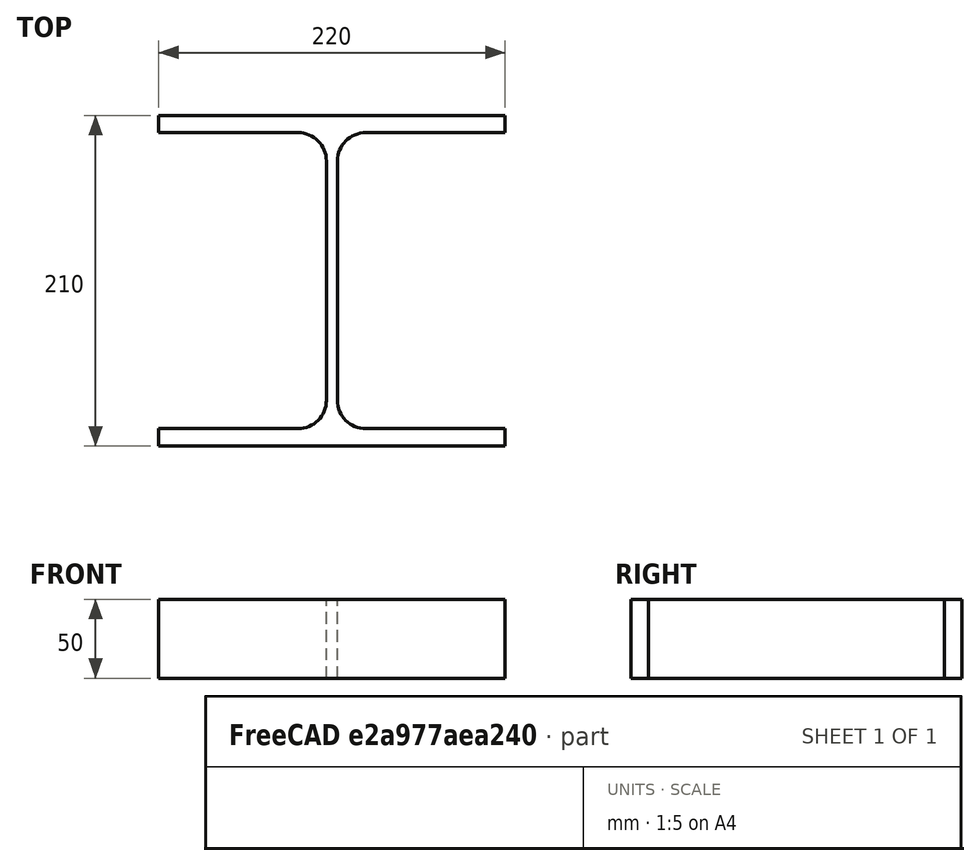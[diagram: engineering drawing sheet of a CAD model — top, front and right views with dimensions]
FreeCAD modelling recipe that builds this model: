
FCSTD DOCUMENT  (FreeCAD 0.15R4671 (Git))
Label: HE-A-Profile 220 DIN1025-3 S235JR
License: All rights reserved
LicenseURL: http://en.wikipedia.org/wiki/All_rights_reserved
objects: Sketcher::SketchObject×1, Part::Extrusion×1
note: 2 computed .brp shape members not serialized (recipe doc carries the construction recipe); baked Part::Feature solids carry a one-line shape summary decoded from their .brp

FEATURE [Sketcher::SketchObject] Sketch
  sketch-geometry (16):
    g0: LineSegment StartX=3.5 StartY=-76 StartZ=0 EndX=3.5 EndY=76 EndZ=0
    g1: LineSegment StartX=21.5 StartY=94 StartZ=0 EndX=110 EndY=94 EndZ=0
    g2: LineSegment StartX=110 StartY=94 StartZ=0 EndX=110 EndY=105 EndZ=0
    g3: LineSegment StartX=110 StartY=105 StartZ=0 EndX=-110 EndY=105 EndZ=0
    g4: LineSegment StartX=-110 StartY=105 StartZ=0 EndX=-110 EndY=94 EndZ=0
    g5: LineSegment StartX=-110 StartY=94 StartZ=0 EndX=-21.5 EndY=94 EndZ=0
    g6: LineSegment StartX=-3.5 StartY=76 StartZ=0 EndX=-3.5 EndY=-76 EndZ=0
    g7: LineSegment StartX=-21.5 StartY=-94 StartZ=0 EndX=-110 EndY=-94 EndZ=0
    g8: LineSegment StartX=-110 StartY=-94 StartZ=0 EndX=-110 EndY=-105 EndZ=0
    g9: LineSegment StartX=-110 StartY=-105 StartZ=0 EndX=110 EndY=-105 EndZ=0
    g10: LineSegment StartX=110 StartY=-105 StartZ=0 EndX=110 EndY=-94 EndZ=0
    g11: LineSegment StartX=110 StartY=-94 StartZ=0 EndX=21.5 EndY=-94 EndZ=0
    g12: ArcOfCircle CenterX=21.5 CenterY=76 CenterZ=0 NormalX=0 NormalY=0 NormalZ=1 Radius=18 StartAngle=1.5708 EndAngle=3.14159
    g13: ArcOfCircle CenterX=21.5 CenterY=-76 CenterZ=0 NormalX=0 NormalY=0 NormalZ=1 Radius=18 StartAngle=3.14159 EndAngle=4.71239
    g14: ArcOfCircle CenterX=-21.5 CenterY=76 CenterZ=0 NormalX=0 NormalY=0 NormalZ=1 Radius=18 StartAngle=0 EndAngle=1.5708
    g15: ArcOfCircle CenterX=-21.5 CenterY=-76 CenterZ=0 NormalX=0 NormalY=0 NormalZ=1 Radius=18 StartAngle=4.71239 EndAngle=6.28319
  constraints (42):
    c: Vertical(g0)
    c: Coincident(g2,g1)
    c: Vertical(g2)
    c: Coincident(g3,g2)
    c: Coincident(g4,g3)
    c: Vertical(g4)
    c: Coincident(g5,g4)
    c: Horizontal(g5)
    c: Vertical(g6)
    c: Horizontal(g7)
    c: Coincident(g8,g7)
    c: Vertical(g8)
    c: Coincident(g9,g8)
    c: Horizontal(g9)
    c: Coincident(g10,g9)
    c: Vertical(g10)
    c: Coincident(g11,g10)
    c: Horizontal(g11)
    c: Tangent(g1,g12) = 1.5708
    c: Tangent(g0,g12) = 1.5708
    c: Tangent(g0,g13) = 1.5708
    c: Tangent(g11,g13) = 1.5708
    c: Tangent(g5,g14) = 1.5708
    c: Tangent(g6,g14) = 1.5708
    c: Tangent(g6,g15) = 1.5708
    c: Tangent(g7,g15) = 1.5708
    c: Equal(g3,g9)
    c: Equal(g2,g4)
    c: Equal(g4,g8)
    c: Equal(g8,g10)
    c: Equal(g12,g14)
    c: Equal(g14,g15)
    c: Equal(g15,g13)
    c: Symmetric(g2,g3,g-2)
    c: Symmetric(g9,g8,g-2)
    c: Symmetric(g0,g6,g-2)
    c: Symmetric(g2,g9,g-1)
    c: DistanceY(g2,g9) = -210
    c: DistanceX(g3) = -220
    c: DistanceX(g0,g6) = -7
    c: DistanceY(g2) = 11
    c: Radius(g12) = 18
FEATURE [Part::Extrusion] Extrude  label="HE-A-Profile 220 DIN1025-3 S235JR"
  Base = -> Sketch
  Dir = (0,0,50)
  Solid = true
